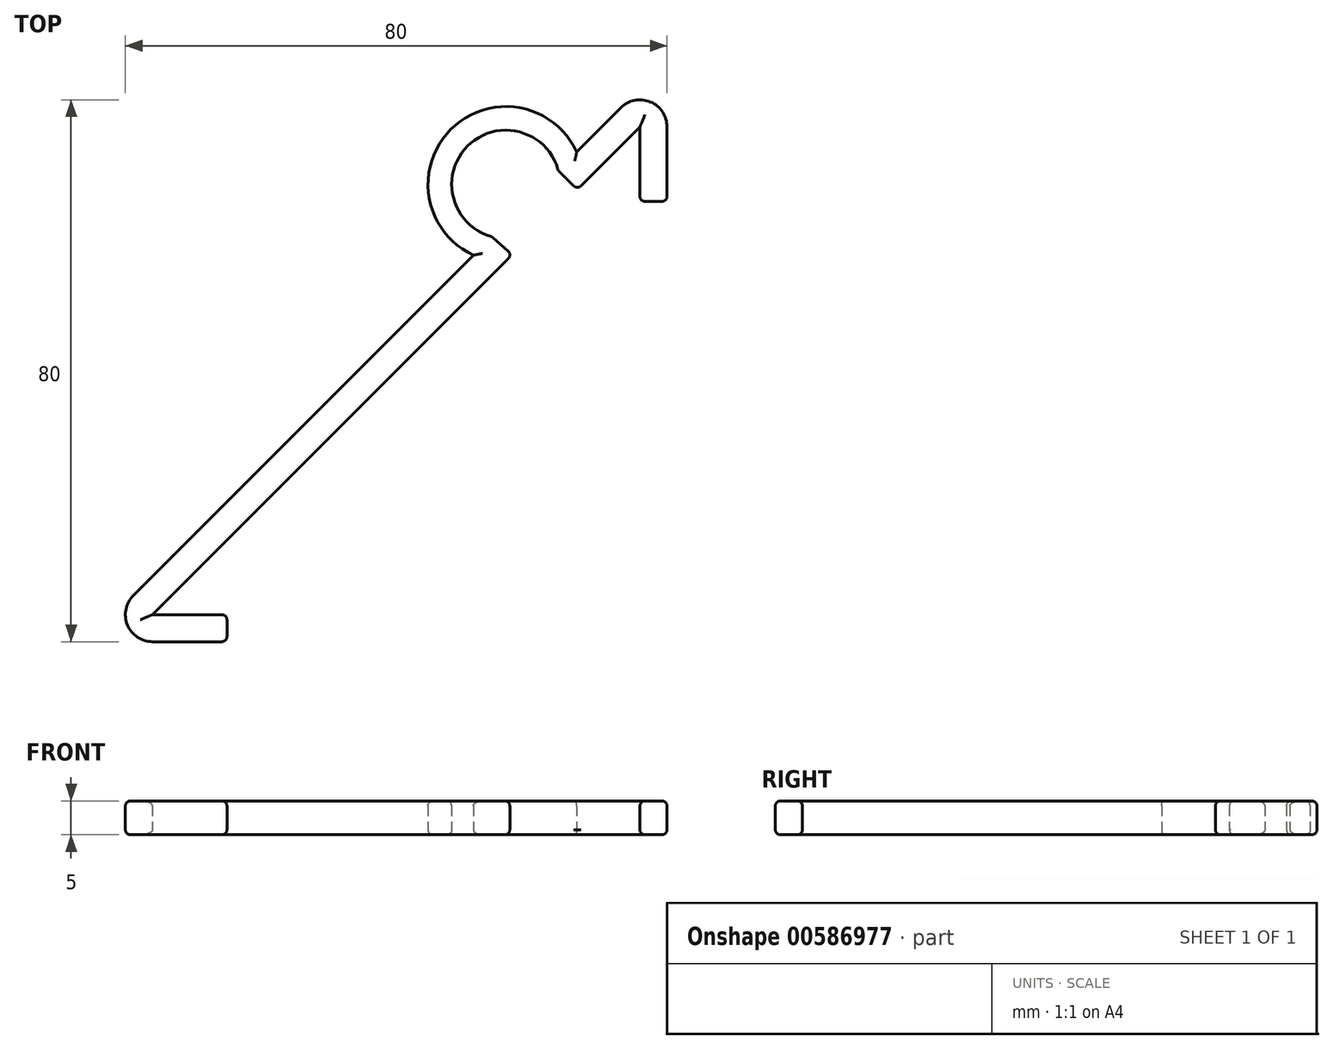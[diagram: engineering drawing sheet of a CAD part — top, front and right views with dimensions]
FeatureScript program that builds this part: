
annotation { "Feature Type Name" : "Feature", "Feature Type Description" : "" }
export const myFeature = defineFeature(function(context is Context, id is Id, definition is map)
    precondition{}
    {
        {
            var Q0;
            Q0=qCreatedBy(makeId("Top.planeOp"),FACE);
            var sketch = newSketch(context, id + "F0", { "sketchPlane" : qUnion([Q0])});
            skLineSegment(sketch, "E0.bottom", {"start": v(36, -36) * mm, "end": v(-36, -36) * mm});
            skLineSegment(sketch, "E0.top", {"start": v(36, 36) * mm, "end": v(-36, 36) * mm, "construction": true});
            skLineSegment(sketch, "E0.left", {"start": v(36, -36) * mm, "end": v(36, 36) * mm});
            skLineSegment(sketch, "E0.right", {"start": v(-36, -36) * mm, "end": v(-36, 36) * mm, "construction": true});
            skPoint(sketch, "E0.middle", {"position": v(0, 0) * mm});
            skLineSegment(sketch, "E1", {"start": v(-36, -36) * mm, "end": v(36, 36) * mm});
            skLineSegment(sketch, "E2.top", {"start": v(36, -40) * mm, "end": v(-36, -40) * mm});
            skLineSegment(sketch, "E2.left", {"start": v(36, -36) * mm, "end": v(36, -40) * mm, "construction": true});
            skLineSegment(sketch, "E2.right", {"start": v(-36, -36) * mm, "end": v(-36, -40) * mm});
            skLineSegment(sketch, "E3.bottom", {"start": v(36, -36) * mm, "end": v(40, -36) * mm});
            skLineSegment(sketch, "E3.top", {"start": v(36, 36) * mm, "end": v(40, 36) * mm});
            skLineSegment(sketch, "E3.right", {"start": v(40, -36) * mm, "end": v(40, 36) * mm});
            skLineSegment(sketch, "E4", {"start": v(-36, -36) * mm, "end": v(-38.83, -33.17) * mm});
            skLineSegment(sketch, "E5", {"start": v(36, 36) * mm, "end": v(33.17, 38.83) * mm});
            skLineSegment(sketch, "E6", {"start": v(33.17, 38.83) * mm, "end": v(-38.83, -33.17) * mm});
            skLineSegment(sketch, "E7.top", {"start": v(36, -36) * mm, "end": v(34, -36) * mm});
            skLineSegment(sketch, "E7.left", {"start": v(36, -40) * mm, "end": v(36, -36) * mm});
            skLineSegment(sketch, "E7.right", {"start": v(34, -39.5) * mm, "end": v(34, -36) * mm, "construction": true});
            skLineSegment(sketch, "E8.bottom", {"start": v(40, -36) * mm, "end": v(36, -36) * mm});
            skLineSegment(sketch, "E8.top", {"start": v(40, -34) * mm, "end": v(36, -34) * mm});
            skLineSegment(sketch, "E8.left", {"start": v(40, -36) * mm, "end": v(40, -34) * mm});
            skLineSegment(sketch, "E8.right", {"start": v(36, -36) * mm, "end": v(36, -34) * mm});
            skLineSegment(sketch, "E9.bottom", {"start": v(36, -36) * mm, "end": v(38.75, -36) * mm});
            skLineSegment(sketch, "E9.left", {"start": v(36, -36) * mm, "end": v(36, -38.75) * mm});
            skLineSegment(sketch, "E10.top", {"start": v(36, -40) * mm, "end": v(40, -40) * mm});
            skLineSegment(sketch, "E10.left", {"start": v(36, -36) * mm, "end": v(36, -40) * mm});
            skLineSegment(sketch, "E10.right", {"start": v(40, -36) * mm, "end": v(40, -40) * mm});
            skLineSegment(sketch, "E11.bottom", {"start": v(40, -40) * mm, "end": v(-25, -40) * mm, "construction": true});
            skLineSegment(sketch, "E11.top", {"start": v(40, -36) * mm, "end": v(-25, -36) * mm, "construction": true});
            skLineSegment(sketch, "E11.left", {"start": v(40, -40) * mm, "end": v(40, -36) * mm, "construction": true});
            skLineSegment(sketch, "E11.right", {"start": v(-25, -40) * mm, "end": v(-25, -36) * mm});
            skLineSegment(sketch, "E12.bottom", {"start": v(40, -40) * mm, "end": v(36, -40) * mm, "construction": true});
            skLineSegment(sketch, "E12.top", {"start": v(40, 25) * mm, "end": v(36, 25) * mm});
            skLineSegment(sketch, "E12.left", {"start": v(40, -40) * mm, "end": v(40, 25) * mm, "construction": true});
            skLineSegment(sketch, "E12.right", {"start": v(36, -40) * mm, "end": v(36, 25) * mm, "construction": true});
            skArc(sketch, "E13", {"start": v(-38.83, -33.17) * mm, "mid": v(-39.7, -37.53) * mm, "end": v(-36, -40) * mm});
            skArc(sketch, "E14", {"start": v(40, 36) * mm, "mid": v(37.53, 39.7) * mm, "end": v(33.17, 38.83) * mm});
            skLineSegment(sketch, "E15", {"start": v(33.17, 38.83) * mm, "end": v(19.03, 24.69) * mm});
            skLineSegment(sketch, "E16", {"start": v(19.03, 24.69) * mm, "end": v(16.2, 27.51) * mm});
            skCircle(sketch, "E17", {"center": v(16.2, 27.51) * mm, "radius": 8 * mm});
            skCircle(sketch, "E18", {"center": v(16.2, 27.51) * mm, "radius": 11.5 * mm});
            skLineSegment(sketch, "E19", {"start": v(14.13, 19.79) * mm, "end": v(17.13, 17.13) * mm});
            skLineSegment(sketch, "E20", {"start": v(23.93, 29.59) * mm, "end": v(26.76, 26.76) * mm});
            skSolve(sketch);
        }
        {
            var Q0;
            {var subQ0=sQuery(id+"F0.wireOp",EDGE,"E2.right");Q0=makeQuery(id+"F0.imprint","IMPRINT",FACE,{"disambiguationData":[TD([[makeQuery(id+"F0.imprint","IMPRINT",EDGE,{"derivedFrom":subQ0}),1.0]])]});}
            var Q1;
            Q1=makeQuery(id+"F0.imprint","IMPRINT",FACE,{"disambiguationData":[TD([[makeQuery(id+"F0.imprint","IMPRINT",EDGE,{"derivedFrom":sQuery(id+"F0.wireOp",EDGE,"E2.right")}),-1.0]])]});
            var Q2;
            {var subQ0=sQuery(id+"F0.wireOp",EDGE,"E4");Q2=makeQuery(id+"F0.imprint","IMPRINT",FACE,{"disambiguationData":[TD([[makeQuery(id+"F0.imprint","IMPRINT",EDGE,{"derivedFrom":subQ0}),-1.0]])]});}
            var Q3;
            {var subQ0=sQuery(id+"F0.wireOp",EDGE,"WVOrYi36-ya93-APVf-Wcgb-ISDxRlG8rq0Z");var subQ1=sQuery(id+"F0.wireOp",EDGE,"E1");var subQ2=makeQuery(id+"F0.imprint","INTERSECT",VERTEX,{"disambiguationData":[OD(0.0)],"derivedFrom":[subQ1,subQ0]});Q3=makeQuery(id+"F0.imprint","IMPRINT",FACE,{"disambiguationData":[TD([[makeQuery(id+"F0.imprint","IMPRINT",EDGE,{"disambiguationData":[TD([[subQ2,-1.0]])],"derivedFrom":subQ1}),1.0]])]});}
            var Q4;
            {var subQ3=sQuery(id+"F0.wireOp",EDGE,"lMZDpXN5-mbea-crBG-5zCS-hbBo6zQeP4cD");var subQ5=sQuery(id+"F0.wireOp",EDGE,"E1");var subQ6=makeQuery(id+"F0.imprint","INTERSECT",VERTEX,{"disambiguationData":[OD(0.0)],"derivedFrom":[subQ5,subQ3]});Q4=makeQuery(id+"F0.imprint","IMPRINT",FACE,{"disambiguationData":[TD([[makeQuery(id+"F0.imprint","IMPRINT",EDGE,{"disambiguationData":[TD([[subQ6,-1.0]])],"derivedFrom":subQ5}),1.0]])]});}
            var Q5;
            {var subQ0=sQuery(id+"F0.wireOp",EDGE,"lMZDpXN5-mbea-crBG-5zCS-hbBo6zQeP4cD");var subQ1=sQuery(id+"F0.wireOp",EDGE,"E1");var subQ2=makeQuery(id+"F0.imprint","INTERSECT",VERTEX,{"disambiguationData":[OD(1.0)],"derivedFrom":[subQ1,subQ0]});Q5=makeQuery(id+"F0.imprint","IMPRINT",FACE,{"disambiguationData":[TD([[makeQuery(id+"F0.imprint","IMPRINT",EDGE,{"disambiguationData":[TD([[subQ2,-1.0]])],"derivedFrom":subQ1}),1.0]])]});}
            var Q6;
            {var subQ0=sQuery(id+"F0.wireOp",EDGE,"E5");Q6=makeQuery(id+"F0.imprint","IMPRINT",FACE,{"disambiguationData":[TD([[makeQuery(id+"F0.imprint","IMPRINT",EDGE,{"derivedFrom":subQ0}),1.0]])]});}
            var Q7;
            Q7=makeQuery(id+"F0.imprint","IMPRINT",FACE,{"disambiguationData":[TD([[makeQuery(id+"F0.imprint","IMPRINT",EDGE,{"derivedFrom":sQuery(id+"F0.wireOp",EDGE,"E3.top")}),1.0]])]});
            var Q8;
            {var subQ0=sQuery(id+"F0.wireOp",EDGE,"E3.top");Q8=makeQuery(id+"F0.imprint","IMPRINT",FACE,{"disambiguationData":[TD([[makeQuery(id+"F0.imprint","IMPRINT",EDGE,{"derivedFrom":subQ0}),-1.0]])]});}
            var Q9;
            {var subQ0=sQuery(id+"F0.wireOp",EDGE,"WVOrYi36-ya93-APVf-Wcgb-ISDxRlG8rq0Z");var subQ1=sQuery(id+"F0.wireOp",EDGE,"E6");var subQ2=makeQuery(id+"F0.imprint","INTERSECT",VERTEX,{"derivedFrom":[subQ1,subQ0]});Q9=makeQuery(id+"F0.imprint","IMPRINT",FACE,{"disambiguationData":[TD([[makeQuery(id+"F0.imprint","IMPRINT",EDGE,{"disambiguationData":[TD([[subQ2,1.0]])],"derivedFrom":subQ1}),-1.0]])]});}
            var Q10;
            {var subQ0=sQuery(id+"F0.wireOp",EDGE,"E19");Q10=makeQuery(id+"F0.imprint","IMPRINT",FACE,{"disambiguationData":[TD([[makeQuery(id+"F0.imprint","IMPRINT",EDGE,{"derivedFrom":subQ0}),-1.0]])]});}
            var Q11;
            {var subQ0=sQuery(id+"F0.wireOp",EDGE,"E20");Q11=makeQuery(id+"F0.imprint","IMPRINT",FACE,{"disambiguationData":[TD([[makeQuery(id+"F0.imprint","IMPRINT",EDGE,{"derivedFrom":subQ0}),1.0]])]});}
            extrude(context, id + "F1", {"entities" : qUnion([Q0, Q1, Q2, Q3, Q4, Q5, Q6, Q7, Q8, Q9, Q10, Q11]), "depth" : 5 * mm, "offsetDistance" : 25 * mm});
        }
        {
            var Q0;
            Q0=makeQuery(id+"F1.opExtrude","CAP_EDGE",EDGE,{"disambiguationData":[OSD([sQuery(id+"F0.wireOp",EDGE,"lMZDpXN5-mbea-crBG-5zCS-hbBo6zQeP4cD")])],"isStart":false});
            var Q1;
            Q1=makeQuery(id+"F1.opExtrude","CAP_EDGE",EDGE,{"disambiguationData":[OSD([sQuery(id+"F0.wireOp",EDGE,"WVOrYi36-ya93-APVf-Wcgb-ISDxRlG8rq0Z")])],"isStart":false});
            var Q2;
            Q2=makeQuery(id+"F1.opExtrude","CAP_EDGE",EDGE,{"disambiguationData":[OSD([sQuery(id+"F0.wireOp",EDGE,"WVOrYi36-ya93-APVf-Wcgb-ISDxRlG8rq0Z")])],"isStart":true});
            var Q3;
            Q3=makeQuery(id+"F1.opExtrude","CAP_EDGE",EDGE,{"disambiguationData":[OSD([sQuery(id+"F0.wireOp",EDGE,"lMZDpXN5-mbea-crBG-5zCS-hbBo6zQeP4cD")])],"isStart":true});
            var Q4;
            Q4=makeQuery(id+"F1.opExtrude","CAP_EDGE",EDGE,{"disambiguationData":[OSD([sQuery(id+"F0.wireOp",EDGE,"E6"),sQuery(id+"F0.wireOp",EDGE,"E15")])],"isStart":true});
            var Q5;
            Q5=makeQuery(id+"F1.opExtrude","CAP_EDGE",EDGE,{"disambiguationData":[OSD([sQuery(id+"F0.wireOp",EDGE,"E6"),sQuery(id+"F0.wireOp",EDGE,"E15")])],"isStart":false});
            var Q6;
            Q6=makeQuery(id+"F1.opExtrude","CAP_EDGE",EDGE,{"disambiguationData":[OSD([sQuery(id+"F0.wireOp",EDGE,"E15")])],"isStart":false});
            var Q7;
            Q7=makeQuery(id+"F1.opExtrude","CAP_FACE",FACE,{"disambiguationData":[OSD([sQuery(id+"F0.wireOp",EDGE,"E1"),sQuery(id+"F0.wireOp",EDGE,"E0.bottom"),sQuery(id+"F0.wireOp",EDGE,"E2.top"),sQuery(id+"F0.wireOp",EDGE,"E0.left"),sQuery(id+"F0.wireOp",EDGE,"E3.right"),sQuery(id+"F0.wireOp",EDGE,"E6"),sQuery(id+"F0.wireOp",EDGE,"E11.right"),sQuery(id+"F0.wireOp",EDGE,"E12.top"),sQuery(id+"F0.wireOp",EDGE,"E13"),sQuery(id+"F0.wireOp",EDGE,"E14"),sQuery(id+"F0.wireOp",EDGE,"E15"),sQuery(id+"F0.wireOp",EDGE,"WVOrYi36-ya93-APVf-Wcgb-ISDxRlG8rq0Z"),sQuery(id+"F0.wireOp",EDGE,"lMZDpXN5-mbea-crBG-5zCS-hbBo6zQeP4cD")])],"isStart":true});
            var Q8;
            Q8=makeQuery(id+"F1.opExtrude","CAP_EDGE",EDGE,{"disambiguationData":[OSD([sQuery(id+"F0.wireOp",EDGE,"E0.left")])],"isStart":false});
            var Q9;
            Q9=makeQuery(id+"F1.opExtrude","SWEPT_EDGE",EDGE,{"disambiguationData":[OSD([sQuery(id+"F0.wireOp",EDGE,"E0.left"),sQuery(id+"F0.wireOp",EDGE,"E12.top")])]});
            var Q10;
            Q10=makeQuery(id+"F1.opExtrude","SWEPT_EDGE",EDGE,{"disambiguationData":[OSD([sQuery(id+"F0.wireOp",EDGE,"E3.right"),sQuery(id+"F0.wireOp",EDGE,"E12.top")])]});
            var Q11;
            Q11=makeQuery(id+"F1.opExtrude","CAP_EDGE",EDGE,{"disambiguationData":[OSD([sQuery(id+"F0.wireOp",EDGE,"E12.top")])],"isStart":false});
            var Q12;
            Q12=makeQuery(id+"F1.opExtrude","CAP_EDGE",EDGE,{"disambiguationData":[OSD([sQuery(id+"F0.wireOp",EDGE,"E1")])],"isStart":false});
            var Q13;
            Q13=makeQuery(id+"F1.opExtrude","CAP_EDGE",EDGE,{"disambiguationData":[OSD([sQuery(id+"F0.wireOp",EDGE,"E6")])],"isStart":false});
            var Q14;
            Q14=makeQuery(id+"F1.opExtrude","CAP_EDGE",EDGE,{"disambiguationData":[OSD([sQuery(id+"F0.wireOp",EDGE,"E0.bottom")])],"isStart":false});
            var Q15;
            Q15=makeQuery(id+"F1.opExtrude","SWEPT_EDGE",EDGE,{"disambiguationData":[OSD([sQuery(id+"F0.wireOp",EDGE,"E2.top"),sQuery(id+"F0.wireOp",EDGE,"E11.right")])]});
            var Q16;
            Q16=makeQuery(id+"F1.opExtrude","SWEPT_EDGE",EDGE,{"disambiguationData":[OSD([sQuery(id+"F0.wireOp",EDGE,"E0.bottom"),sQuery(id+"F0.wireOp",EDGE,"E11.right")])]});
            var Q17;
            Q17=makeQuery(id+"F1.opExtrude","CAP_EDGE",EDGE,{"disambiguationData":[OSD([sQuery(id+"F0.wireOp",EDGE,"E0.bottom")])],"isStart":true});
            var Q18;
            Q18=makeQuery(id+"F1.opExtrude","CAP_EDGE",EDGE,{"disambiguationData":[OSD([sQuery(id+"F0.wireOp",EDGE,"E1")])],"isStart":true});
            var Q19;
            Q19=makeQuery(id+"F1.opExtrude","CAP_EDGE",EDGE,{"disambiguationData":[OSD([sQuery(id+"F0.wireOp",EDGE,"E11.right")])],"isStart":false});
            var Q20;
            Q20=makeQuery(id+"F1.opExtrude","SWEPT_EDGE",EDGE,{"disambiguationData":[OSD([sQuery(id+"F0.wireOp",EDGE,"E15"),sQuery(id+"F0.wireOp",EDGE,"E17"),sQuery(id+"F0.wireOp",EDGE,"E20")])]});
            var Q21;
            Q21=makeQuery(id+"F1.opExtrude","SWEPT_EDGE",EDGE,{"disambiguationData":[OSD([sQuery(id+"F0.wireOp",EDGE,"E1"),sQuery(id+"F0.wireOp",EDGE,"E20")])]});
            var Q22;
            Q22=makeQuery(id+"F1.opExtrude","SWEPT_EDGE",EDGE,{"disambiguationData":[OSD([sQuery(id+"F0.wireOp",EDGE,"E1"),sQuery(id+"F0.wireOp",EDGE,"E19")])]});
            var Q23;
            Q23=makeQuery(id+"F1.opExtrude","SWEPT_EDGE",EDGE,{"disambiguationData":[OSD([sQuery(id+"F0.wireOp",EDGE,"E6"),sQuery(id+"F0.wireOp",EDGE,"E17"),sQuery(id+"F0.wireOp",EDGE,"E19")])]});
            var Q24;
            Q24=makeQuery(id+"F1.opExtrude","CAP_EDGE",EDGE,{"disambiguationData":[OSD([sQuery(id+"F0.wireOp",EDGE,"E18")])],"isStart":false});
            var Q25;
            Q25=makeQuery(id+"F1.opExtrude","CAP_EDGE",EDGE,{"disambiguationData":[OSD([sQuery(id+"F0.wireOp",EDGE,"E19")])],"isStart":false});
            var Q26;
            Q26=makeQuery(id+"F1.opExtrude","CAP_EDGE",EDGE,{"disambiguationData":[OSD([sQuery(id+"F0.wireOp",EDGE,"E20")])],"isStart":false});
            var Q27;
            Q27=makeQuery(id+"F1.opExtrude","CAP_EDGE",EDGE,{"disambiguationData":[OSD([sQuery(id+"F0.wireOp",EDGE,"E17")])],"isStart":false});
            fillet(context, id + "F2", {"entities" : qUnion([Q0, Q1, Q2, Q3, Q4, Q5, Q6, Q7, Q8, Q9, Q10, Q11, Q12, Q13, Q14, Q15, Q16, Q17, Q18, Q19, Q20, Q21, Q22, Q23, Q24, Q25, Q26, Q27]), "radius" : .75 * mm, "tangentPropagation" : true, "allowEdgeOverflow" : false});
        }
    });
